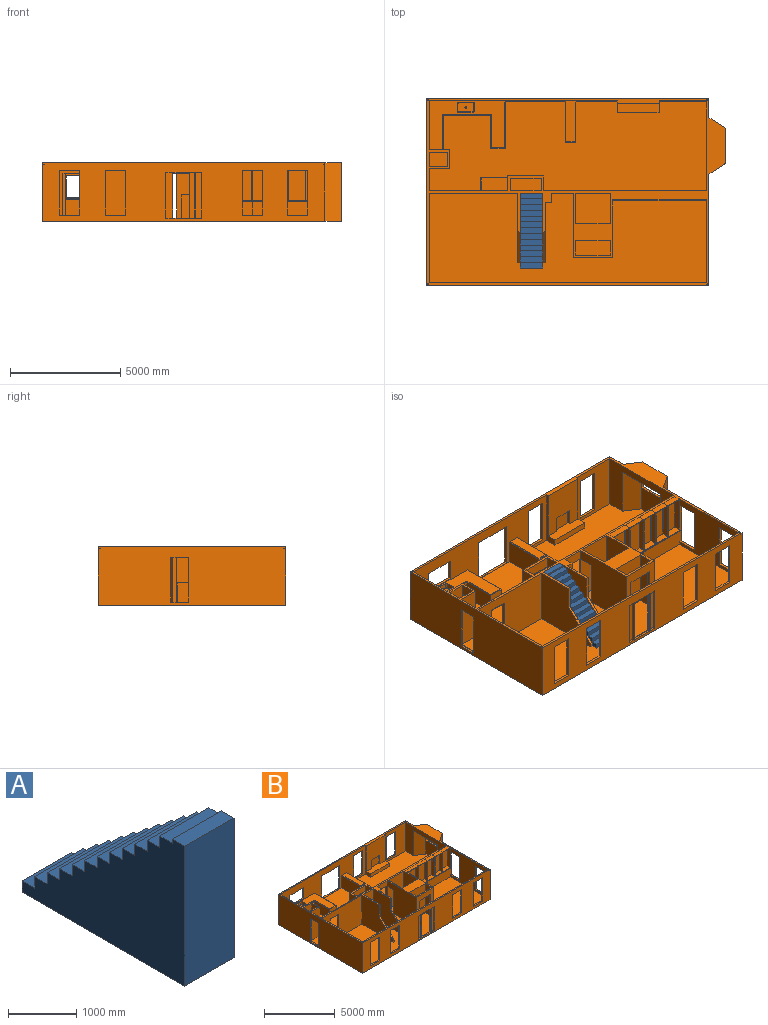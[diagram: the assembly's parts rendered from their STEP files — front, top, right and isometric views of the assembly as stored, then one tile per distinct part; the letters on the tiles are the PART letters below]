
ASSEMBLY  parts=2 mates=1
PART A: 30 faces, bbox 1019.2x3384.6x2514.6 mm
  f0: plane 1019.18x203.2mm, normal (0,1,0), area 207096.4mm2, adj f1,f3,f5,f6
  f1: plane 3384.55x2514.6mm, normal (-1,0,0), area 4781119.5mm2, adj f0,f2,f4,f5,f6,f7,f8,f9
  f2: plane 2514.6x1019.18mm, normal (0,-1,0), area 2562817.5mm2, adj f1,f3,f4,f5
  f3: plane 3384.55x2514.6mm, normal (1,0,0), area 4781119.5mm2, adj f0,f2,f4,f5,f6,f7,f8,f9
  f4: plane 1019.18x260.35mm, normal (0,0,1), area 265342.2mm2, adj f1,f2,f3,f7
  f5: plane 3384.55x1019.18mm, normal (0,0,-1), area 3449448.7mm2, adj f0,f1,f2,f3
  f6: plane 1019.18x260.35mm, normal (0,0,1), area 265342.2mm2, adj f0,f1,f3,f29
  f7: plane 1019.18x76.2mm, normal (0,1,0), area 77661.1mm2, adj f1,f3,f4,f8
  f8: plane 1019.18x260.35mm, normal (0,0,1), area 265342.2mm2, adj f1,f3,f7,f9
  f9: plane 1019.18x203.2mm, normal (0,1,0), area 207096.4mm2, adj f1,f3,f8,f10
  f10: plane 1019.18x260.35mm, normal (0,0,1), area 265342.2mm2, adj f1,f3,f9,f11
  f11: plane 1019.18x203.2mm, normal (0,1,0), area 207096.4mm2, adj f1,f3,f10,f12
  f12: plane 1019.18x260.35mm, normal (0,0,1), area 265342.2mm2, adj f1,f3,f11,f13
  f13: plane 1019.18x203.2mm, normal (0,1,0), area 207096.4mm2, adj f1,f3,f12,f14
  f14: plane 1019.18x260.35mm, normal (0,0,1), area 265342.2mm2, adj f1,f3,f13,f15
  f15: plane 1019.18x203.2mm, normal (0,1,0), area 207096.4mm2, adj f1,f3,f14,f16
  f16: plane 1019.18x260.35mm, normal (0,0,1), area 265342.2mm2, adj f1,f3,f15,f17
  f17: plane 1019.18x203.2mm, normal (0,1,0), area 207096.4mm2, adj f1,f3,f16,f18
  f18: plane 1019.18x260.35mm, normal (0,0,1), area 265342.2mm2, adj f1,f3,f17,f19
  f19: plane 1019.18x203.2mm, normal (0,1,0), area 207096.4mm2, adj f1,f3,f18,f20
  f20: plane 1019.18x260.35mm, normal (0,0,1), area 265342.2mm2, adj f1,f3,f19,f21
  f21: plane 1019.18x203.2mm, normal (0,1,0), area 207096.4mm2, adj f1,f3,f20,f22
  f22: plane 1019.18x260.35mm, normal (0,0,1), area 265342.2mm2, adj f1,f3,f21,f23
  f23: plane 1019.18x203.2mm, normal (0,1,0), area 207096.4mm2, adj f1,f3,f22,f24
  f24: plane 1019.18x260.35mm, normal (0,0,1), area 265342.2mm2, adj f1,f3,f23,f25
  f25: plane 1019.18x203.2mm, normal (0,1,0), area 207096.4mm2, adj f1,f3,f24,f26
  f26: plane 1019.18x260.35mm, normal (0,0,1), area 265342.2mm2, adj f1,f3,f25,f27
  f27: plane 1019.18x203.2mm, normal (0,1,0), area 207096.4mm2, adj f1,f3,f26,f28
  f28: plane 1019.18x260.35mm, normal (0,0,1), area 265342.2mm2, adj f1,f3,f27,f29
  f29: plane 1019.18x203.2mm, normal (0,1,0), area 207096.4mm2, adj f1,f3,f6,f28
PART B: 232 faces, bbox 13538.2x8470.9x2628.9 mm
  f0: plane 1695.45x304.8mm, normal (1,0,0), area 516773.2mm2, adj f12,f218,f221,f230
  f1: plane 1695.45x304.8mm, normal (-1,0,0), area 516773.2mm2, adj f55,f218,f221,f231
  f2: plane 1695.45x304.8mm, normal (-1,0,0), area 516773.2mm2, adj f12,f218,f221,f230
  f3: plane 1695.45x304.8mm, normal (1,0,0), area 516773.2mm2, adj f10,f218,f221,f229
  f4: plane 1695.45x304.8mm, normal (-1,0,0), area 516773.2mm2, adj f10,f218,f221,f229
  f5: plane 1695.45x304.8mm, normal (1,0,0), area 516773.2mm2, adj f9,f218,f221,f228
  f6: plane 1695.45x304.8mm, normal (-1,0,0), area 516773.2mm2, adj f9,f218,f221,f228
  f7: plane 1695.45x304.8mm, normal (1,0,0), area 516773.2mm2, adj f8,f218,f221,f227
  f8: plane 1695.45x730.25mm, normal (0,-1,0), area 1238102.2mm2, adj f7,f218,f223,f227
  f9: plane 1695.45x749.3mm, normal (0,-1,0), area 1270400.7mm2, adj f5,f6,f218,f228
  f10: plane 1695.45x736.6mm, normal (0,-1,0), area 1248868.5mm2, adj f3,f4,f218,f229
  f11: plane 2609.85x2514.6mm, normal (1,0,0), area 6561467.4mm2, adj f14,f29,f54,f200,f216,f217,f218,f219
  f12: plane 1695.45x889mm, normal (0,-1,0), area 1507255mm2, adj f0,f2,f218,f230
  f13: plane 3759.2x2514.6mm, normal (-1,0,0), area 5736762.7mm2, adj f14,f26,f29,f198,f199,f201,f202,f203
  f14: plane 13309.6x8242.3mm, normal (0,0,1), area 92807452.3mm2, adj f11,f13,f15,f16,f17,f21,f22,f26
  f15: plane 3568.7x2514.6mm, normal (0,1,0), area 6190955.4mm2, adj f14,f16,f29,f31,f72,f73,f74,f210
  f16: plane 2514.6x666.75mm, normal (-1,0,0), area 1121449.4mm2, adj f14,f15,f29,f63,f211,f212,f213
  f17: plane 1460.5x1171.91mm, normal (-1,0,0), area 1711580mm2, adj f14,f89,f90,f207
  f18: plane 1460.5x62.35mm, normal (-1,0,0), area 91056.8mm2, adj f89,f90,f91,f209
  f19: plane 5043.5x2628.9mm, normal (1,0,0), area 9542743.4mm2, adj f25,f29,f56,f181,f198,f199,f201,f202
  f20: plane 12788.9x2628.9mm, normal (0,1,0), area 24988966mm2, adj f29,f30,f59,f113,f114,f115,f116,f149
  f21: plane 8521.7x2514.6mm, normal (0,-1,0), area 11001332.7mm2, adj f14,f23,f24,f29,f104,f109,f110,f111
  f22: plane 2514.6x2146.3mm, normal (0,-1,0), area 3539025.2mm2, adj f14,f29,f32,f105,f167,f168,f169,f170
  f23: plane 3435.35x2203.45mm, normal (0,0,1), area 3658851.1mm2, adj f21,f24,f60,f158,f159,f160,f161,f163
  f24: plane 2203.45x1612.9mm, normal (1,0,0), area 3553944.5mm2, adj f21,f23,f29,f60
  f25: plane 12788.9x2628.9mm, normal (0,-1,0), area 22922373.5mm2, adj f19,f29,f30,f82,f83,f84,f85,f92
  f26: plane 12560.3x2514.6mm, normal (0,1,0), area 22139955.7mm2, adj f13,f14,f29,f69,f82,f83,f84,f85
  f27: plane 136.53x114.3mm, normal (0,-1,0), area 15604.8mm2, adj f14,f45,f46,f123
  f28: plane 136.53x114.3mm, normal (0,-1,0), area 15604.8mm2, adj f14,f48,f49,f122
  f29: plane 13538.2x8470.9mm, normal (0,0,1), area 12409928.7mm2, adj f11,f13,f15,f16,f19,f20,f21,f22
  f30: plane 8470.9x2628.9mm, normal (-1,0,0), area 20630442.6mm2, adj f20,f25,f29,f117,f118,f119,f120,f181
  f31: plane 2514.6x996.95mm, normal (1,0,0), area 868224.1mm2, adj f14,f15,f29,f64,f117,f118,f119,f120
  f32: plane 4064x2514.6mm, normal (-1,0,0), area 4954828.8mm2, adj f14,f22,f29,f61,f89,f90,f91
  f33: plane 2514.6x863.6mm, normal (1,0,0), area 932901.7mm2, adj f14,f29,f60,f64,f86,f87,f88
  f34: plane 2514.6x1397mm, normal (0,-1,0), area 1087094.6mm2, adj f14,f29,f41,f43,f79,f80,f81
  f35: plane 2514.6x1549.4mm, normal (0,1,0), area 1439997.1mm2, adj f14,f29,f36,f37,f76,f77,f78
  f36: plane 2514.6x647.7mm, normal (-1,0,0), area 1628706.4mm2, adj f14,f29,f35,f71
  f37: plane 2514.6x647.7mm, normal (1,0,0), area 1628706.4mm2, adj f14,f29,f35,f71
  f38: plane 2514.6x1384.3mm, normal (1,0,0), area 2113221.6mm2, adj f14,f29,f39,f68,f102,f103
  f39: plane 2514.6x1663.7mm, normal (0,-1,0), area 4128378.8mm2, adj f14,f29,f38,f40,f53,f103
  f40: plane 2514.6x1384.3mm, normal (-1,0,0), area 3480960.8mm2, adj f14,f29,f39,f68
  f41: plane 2514.6x552.45mm, normal (-1,0,0), area 1389190.8mm2, adj f14,f29,f34,f42
  f42: plane 2514.6x1397mm, normal (0,1,0), area 3512896.2mm2, adj f14,f29,f41,f43
  f43: plane 2514.6x552.45mm, normal (1,0,0), area 1389190.8mm2, adj f14,f29,f34,f42
  f44: plane 4013.2x2514.6mm, normal (0,-1,0), area 8419338mm2, adj f14,f29,f45,f69,f72,f73,f74
  f45: plane 3149.6x2514.6mm, normal (-1,0,0), area 5509767.2mm2, adj f14,f27,f29,f44,f123,f124
  f46: plane 3149.6x2514.6mm, normal (1,0,0), area 5509767.2mm2, adj f14,f27,f29,f47,f123,f124
  f47: plane 2514.6x1022.35mm, normal (0,-1,0), area 2570801.5mm2, adj f14,f29,f46,f48
  f48: plane 3149.6x2514.6mm, normal (-1,0,0), area 5509767.2mm2, adj f14,f28,f29,f47,f121,f122
  f49: plane 2717.8x2514.6mm, normal (1,0,0), area 4423962.9mm2, adj f14,f28,f29,f50,f121,f122
  f50: plane 2514.6x273.05mm, normal (0,-1,0), area 686611.5mm2, adj f14,f29,f49,f51
  f51: plane 2514.6x546.1mm, normal (1,0,0), area 1320965.1mm2, adj f14,f29,f50,f52,f61,f75
  f52: plane 996.95x457.2mm, normal (0,-1,0), area 455805.5mm2, adj f29,f51,f53,f75
  f53: plane 3028.95x2514.6mm, normal (-1,0,0), area 6196600.5mm2, adj f14,f29,f39,f52,f54,f61,f75,f102
  f54: plane 2514.6x1778mm, normal (0,-1,0), area 2014834.7mm2, adj f11,f14,f29,f53,f76,f77,f78
  f55: plane 1695.45x1028.7mm, normal (0,-1,0), area 1744109.4mm2, adj f1,f218,f222,f231
  f56: plane 2628.9x749.3mm, normal (0.55,-0.84,0), area 2352127.5mm2, adj f19,f29,f57,f181
  f57: plane 2628.9x1584.29mm, normal (1,0,0), area 2814367.8mm2, adj f29,f56,f58,f181,f206,f207,f208,f209
  f58: plane 2628.9x749.3mm, normal (0.55,0.84,0), area 2352127.5mm2, adj f29,f57,f59,f181
  f59: plane 2628.9x865.2mm, normal (1,0,0), area 2274532.1mm2, adj f20,f29,f58,f181
  f60: plane 2514.6x915.15mm, normal (0,1,0), area 1728976.2mm2, adj f14,f23,f24,f29,f33,f153,f197
  f61: plane 7366x2514.6mm, normal (0,1,0), area 16471418.7mm2, adj f14,f29,f32,f51,f53,f62,f75
  f62: plane 2514.6x666.75mm, normal (1,0,0), area 1676609.5mm2, adj f14,f29,f61,f63
  f63: plane 2514.6x1625.6mm, normal (0,1,0), area 1661932.2mm2, adj f14,f16,f29,f62,f79,f80,f81
  f64: plane 2514.6x914.4mm, normal (0,-1,0), area 2299350.2mm2, adj f14,f29,f31,f33
  f65: plane 2514.6x826.73mm, normal (0,-1,0), area 2078905.6mm2, adj f14,f29,f66,f70
  f66: plane 2514.6x635mm, normal (-1,0,0), area 358063.8mm2, adj f14,f29,f65,f67,f86,f87,f88
  f67: plane 2514.6x826.73mm, normal (0,1,0), area 2078905.6mm2, adj f14,f29,f66,f70
  f68: plane 2514.6x1549.4mm, normal (0,1,0), area 3896121.2mm2, adj f14,f29,f38,f40
  f69: plane 4064x2514.6mm, normal (1,0,0), area 10219334.4mm2, adj f14,f26,f29,f44
  f70: plane 2514.6x635mm, normal (1,0,0), area 1596771mm2, adj f14,f29,f65,f67
  f71: plane 2514.6x1549.4mm, normal (0,-1,0), area 3896121.2mm2, adj f14,f29,f36,f37
  f72: plane 2057.4x114.3mm, normal (1,0,0), area 235160.8mm2, adj f14,f15,f44,f74
  f73: plane 2057.4x114.3mm, normal (-1,0,0), area 235160.8mm2, adj f14,f15,f44,f74
  f74: plane 812.8x114.3mm, normal (0,0,-1), area 92903mm2, adj f15,f44,f72,f73
  f75: plane 996.95x114.3mm, normal (0,0,-1), area 113951.4mm2, adj f51,f52,f53,f61
  f76: plane 2057.4x114.3mm, normal (1,0,0), area 235160.8mm2, adj f14,f35,f54,f78
  f77: plane 2057.4x114.3mm, normal (-1,0,0), area 235160.8mm2, adj f14,f35,f54,f78
  f78: plane 1193.8x114.3mm, normal (0,0,-1), area 136451.3mm2, adj f35,f54,f76,f77
  f79: plane 2032x114.3mm, normal (-1,0,0), area 232257.6mm2, adj f14,f34,f63,f81
  f80: plane 2032x114.3mm, normal (1,0,0), area 232257.6mm2, adj f14,f34,f63,f81
  f81: plane 1193.8x114.3mm, normal (0,0,-1), area 136451.3mm2, adj f34,f63,f79,f80
  f82: plane 2057.4x114.3mm, normal (1,0,0), area 235160.8mm2, adj f25,f26,f83,f85
  f83: plane 977.9x114.3mm, normal (0,0,1), area 111774mm2, adj f25,f26,f82,f84
  f84: plane 2057.4x114.3mm, normal (-1,0,0), area 235160.8mm2, adj f25,f26,f83,f85
  f85: plane 977.9x114.3mm, normal (0,0,-1), area 111774mm2, adj f25,f26,f82,f84
  f86: plane 2032x87.78mm, normal (0,1,0), area 178360.8mm2, adj f14,f33,f66,f88
  f87: plane 2032x88.3mm, normal (0,-1,0), area 179434.8mm2, adj f14,f33,f66,f88
  f88: plane 609.6x88.3mm, normal (0,0,-1), area 53669.3mm2, adj f33,f66,f86,f87
  f89: plane 2159x749.3mm, normal (-0.55,0.84,0), area 1931698.9mm2, adj f14,f17,f18,f32,f91,f208
  f90: plane 2159x749.3mm, normal (-0.55,-0.84,0), area 1931698.9mm2, adj f14,f17,f18,f32,f91,f206
  f91: plane 2438.4x749.3mm, normal (0,0,-1), area 1460722.9mm2, adj f18,f32,f89,f90
  f92: plane 304.8x101.6mm, normal (0,0,-1), area 30967.7mm2, adj f25,f93,f95,f96
  f93: plane 2057.4x101.6mm, normal (1,0,0), area 209031.8mm2, adj f25,f92,f94,f96
  f94: plane 304.8x101.6mm, normal (0,0,1), area 30967.7mm2, adj f25,f93,f95,f96
  f95: plane 2057.4x101.6mm, normal (-1,0,0), area 209031.8mm2, adj f25,f92,f94,f96
  f96: plane 2057.4x304.8mm, normal (0,-1,0), area 627095.5mm2, adj f92,f93,f94,f95
  f97: plane 304.8x101.6mm, normal (0,0,1), area 30967.7mm2, adj f25,f98,f100,f101
  f98: plane 2057.4x101.6mm, normal (-1,0,0), area 209031.8mm2, adj f25,f97,f99,f101
  f99: plane 304.8x101.6mm, normal (0,0,-1), area 30967.7mm2, adj f25,f98,f100,f101
  f100: plane 2057.4x101.6mm, normal (1,0,0), area 209031.8mm2, adj f25,f97,f99,f101
  f101: plane 2057.4x304.8mm, normal (0,-1,0), area 627095.5mm2, adj f97,f98,f99,f100
  f102: plane 2032x114.3mm, normal (0,1,0), area 232257.6mm2, adj f14,f38,f53,f103
  f103: plane 673.1x114.3mm, normal (0,0,-1), area 76935.3mm2, adj f38,f39,f53,f102
  f104: plane 2514.6x533.4mm, normal (-1,0,0), area 393023.4mm2, adj f14,f21,f29,f106,f107,f108
  f105: plane 2514.6x533.4mm, normal (1,0,0), area 393023.4mm2, adj f14,f22,f29,f106,f107,f108
  f106: plane 2228.85x1892.3mm, normal (0,-1,0), area 3618107.4mm2, adj f29,f104,f105,f107,f186,f187,f188
  f107: plane 1892.3x527.05mm, normal (0,0,1), area 888949.8mm2, adj f104,f105,f106,f108,f186,f188,f189
  f108: plane 1892.3x285.75mm, normal (0,-1,0), area 540724.7mm2, adj f14,f104,f105,f107
  f109: plane 1866.9x1066.8mm, normal (1,0,0), area 1991608.9mm2, adj f14,f21,f112,f192
  f110: plane 1841.5x438.15mm, normal (0,0,1), area 806853.2mm2, adj f21,f190,f191,f192
  f111: plane 1866.9x1066.8mm, normal (-1,0,0), area 1991608.9mm2, adj f14,f21,f112,f190
  f112: plane 1066.8x488.95mm, normal (0,-1,0), area 521611.9mm2, adj f14,f109,f111,f191
  f113: plane 1787.53x114.3mm, normal (0,0,1), area 204314.1mm2, adj f20,f21,f114,f116
  f114: plane 2012.95x114.3mm, normal (-1,0,0), area 230080.2mm2, adj f20,f21,f113,f115
  f115: plane 1787.53x114.3mm, normal (0,0,-1), area 204314.1mm2, adj f20,f21,f114,f116
  f116: plane 2012.95x114.3mm, normal (1,0,0), area 230080.2mm2, adj f20,f21,f113,f115
  f117: plane 2032x114.3mm, normal (0,-1,0), area 232257.6mm2, adj f30,f31,f118,f120
  f118: plane 806.45x114.3mm, normal (0,0,-1), area 92177.2mm2, adj f30,f31,f117,f119
  f119: plane 2032x114.3mm, normal (0,1,0), area 232257.6mm2, adj f30,f31,f118,f120
  f120: plane 806.45x114.3mm, normal (0,0,1), area 92177.2mm2, adj f30,f31,f117,f119
  f121: plane 1041.4x114.3mm, normal (0,-1,0), area 119032mm2, adj f29,f48,f49,f122
  f122: plane 1409.7x1336.68mm, normal (0,-0.69,0.73), area 222046.8mm2, adj f28,f48,f49,f121
  f123: plane 1409.7x1336.68mm, normal (0,-0.69,0.73), area 222046.8mm2, adj f27,f45,f46,f124
  f124: plane 1041.4x114.3mm, normal (0,-1,0), area 119032mm2, adj f29,f45,f46,f123
  f125: cylinder r=31.75mm len=63.5mm, axis (0,0,1), area 10134.1mm2, adj f29,f126
  f126: plane 63.5x63.5mm, normal (0,0,1), area 3166.9mm2, adj f125
  f127: cylinder r=31.75mm len=63.5mm, axis (0,0,1), area 10134.1mm2, adj f29,f128
  f128: plane 63.5x63.5mm, normal (0,0,1), area 3166.9mm2, adj f127
  f129: cylinder r=31.75mm len=63.5mm, axis (0,0,1), area 10134.1mm2, adj f29,f130
  f130: plane 63.5x63.5mm, normal (0,0,1), area 3166.9mm2, adj f129
  f131: cylinder r=31.75mm len=63.5mm, axis (0,0,1), area 10134.1mm2, adj f29,f132
  f132: plane 63.5x63.5mm, normal (0,0,1), area 3166.9mm2, adj f131
  f133: plane 914.4x114.3mm, normal (0,0,1), area 104515.9mm2, adj f25,f26,f134,f136
  f134: plane 2032x114.3mm, normal (1,0,0), area 232257.6mm2, adj f25,f26,f133,f135
  f135: plane 914.4x114.3mm, normal (0,0,-1), area 104515.9mm2, adj f25,f26,f134,f136
  f136: plane 2032x114.3mm, normal (-1,0,0), area 232257.6mm2, adj f25,f26,f133,f135
  f137: plane 914.4x114.3mm, normal (0,0,-1), area 104515.9mm2, adj f25,f26,f138,f140
  f138: plane 2032x114.3mm, normal (-1,0,0), area 232257.6mm2, adj f25,f26,f137,f139
  f139: plane 914.4x114.3mm, normal (0,0,1), area 104515.9mm2, adj f25,f26,f138,f140
  f140: plane 2032x114.3mm, normal (1,0,0), area 232257.6mm2, adj f25,f26,f137,f139
  f141: plane 914.4x114.3mm, normal (0,0,-1), area 104515.9mm2, adj f25,f26,f142,f144
  f142: plane 2032x114.3mm, normal (-1,0,0), area 232257.6mm2, adj f25,f26,f141,f143
  f143: plane 914.4x114.3mm, normal (0,0,1), area 104515.9mm2, adj f25,f26,f142,f144
  f144: plane 2032x114.3mm, normal (1,0,0), area 232257.6mm2, adj f25,f26,f141,f143
  f145: plane 2032x114.3mm, normal (1,0,0), area 232257.6mm2, adj f25,f26,f146,f148
  f146: plane 914.4x114.3mm, normal (0,0,-1), area 104515.9mm2, adj f25,f26,f145,f147
  f147: plane 2032x114.3mm, normal (-1,0,0), area 232257.6mm2, adj f25,f26,f146,f148
  f148: plane 914.4x114.3mm, normal (0,0,1), area 104515.9mm2, adj f25,f26,f145,f147
  f149: plane 1377.95x114.3mm, normal (0,0,-1), area 157499.7mm2, adj f20,f21,f150,f152
  f150: plane 960.78x114.3mm, normal (1,0,0), area 109817mm2, adj f20,f21,f149,f151
  f151: plane 1377.95x114.3mm, normal (0,0,1), area 157499.7mm2, adj f20,f21,f150,f152
  f152: plane 960.78x114.3mm, normal (-1,0,0), area 109817mm2, adj f20,f21,f149,f151
  f153: plane 1568.45x876.3mm, normal (1,0,0), area 1374432.7mm2, adj f14,f60,f155,f197
  f154: plane 2146.3x876.3mm, normal (1,0,0), area 1880802.7mm2, adj f14,f21,f157,f193
  f155: plane 2149.48x876.3mm, normal (0,-1,0), area 1883584.9mm2, adj f14,f153,f156,f196
  f156: plane 1511.3x876.3mm, normal (-1,0,0), area 1324352.2mm2, adj f14,f155,f157,f195
  f157: plane 876.3x676.28mm, normal (0,-1,0), area 592619.8mm2, adj f14,f154,f156,f194
  f158: plane 324.73x228.6mm, normal (1,0,0), area 74232.9mm2, adj f23,f163,f166,f176
  f159: plane 660.4x228.6mm, normal (0,1,0), area 150967.4mm2, adj f23,f163,f164,f177
  f160: plane 324.73x228.6mm, normal (-1,0,0), area 74232.9mm2, adj f23,f164,f165,f173
  f161: plane 660.4x228.6mm, normal (0,-1,0), area 150967.4mm2, adj f23,f165,f166,f172
  f162: plane 736.6x400.93mm, normal (0,0,1), area 289517.4mm2, adj f171,f172,f173,f174,f175,f176,f177,f178
  f163: cylinder r=63.5mm len=228.6mm, axis (0,0,1), area 22801.8mm2, adj f23,f158,f159,f178
  f164: cylinder r=63.5mm len=228.6mm, axis (0,0,-1), area 22801.8mm2, adj f23,f159,f160,f175
  f165: cylinder r=63.5mm len=228.6mm, axis (0,0,1), area 22801.8mm2, adj f23,f160,f161,f171
  f166: cylinder r=63.5mm len=228.6mm, axis (0,0,-1), area 22801.8mm2, adj f23,f158,f161,f174
  f167: plane 2032x114.3mm, normal (-1,0,0), area 232257.6mm2, adj f20,f22,f168,f170
  f168: plane 914.4x114.3mm, normal (0,0,-1), area 104515.9mm2, adj f20,f22,f167,f169
  f169: plane 2032x114.3mm, normal (1,0,0), area 232257.6mm2, adj f20,f22,f168,f170
  f170: plane 914.4x114.3mm, normal (0,0,1), area 104515.9mm2, adj f20,f22,f167,f169
  f171: torus R=38.1mm, axis (0,0,1), area 3401.2mm2, adj f162,f165,f172,f173
  f172: cylinder r=25.4mm len=660.4mm, axis (-1,0,0), area 26348.8mm2, adj f161,f162,f171,f174
  f173: cylinder r=25.4mm len=324.73mm, axis (0,1,0), area 12956.1mm2, adj f160,f162,f171,f175
  f174: torus R=38.1mm, axis (0,0,1), area 3401.2mm2, adj f162,f166,f172,f176
  f175: torus R=38.1mm, axis (0,0,1), area 3401.2mm2, adj f162,f164,f173,f177
  f176: cylinder r=25.4mm len=324.73mm, axis (0,-1,0), area 12956.1mm2, adj f158,f162,f174,f178
  f177: cylinder r=25.4mm len=660.4mm, axis (1,0,0), area 26348.8mm2, adj f159,f162,f175,f178
  f178: torus R=38.1mm, axis (0,0,1), area 3401.2mm2, adj f162,f163,f176,f177
  f179: cylinder r=38.1mm len=76.2mm, axis (0,0,1), area 6080.5mm2, adj f162,f180
  f180: plane 76.2x76.2mm, normal (0,0,1), area 4560.4mm2, adj f179
  f181: plane 13538.2x8470.9mm, normal (0,0,-1), area 109886974.8mm2, adj f19,f20,f25,f30,f56,f57,f58,f59
  f182: plane 2032x114.3mm, normal (1,0,0), area 232257.6mm2, adj f20,f21,f183,f185
  f183: plane 911.23x114.3mm, normal (0,0,1), area 104153mm2, adj f20,f21,f182,f184
  f184: plane 2032x114.3mm, normal (-1,0,0), area 232257.6mm2, adj f20,f21,f183,f185
  f185: plane 911.23x114.3mm, normal (0,0,-1), area 104153mm2, adj f20,f21,f182,f184
  f186: plane 726.28x101.6mm, normal (-1,0,0), area 73790.2mm2, adj f106,f107,f187,f189
  f187: plane 825.5x101.6mm, normal (0,0,-1), area 83870.8mm2, adj f106,f186,f188,f189
  f188: plane 726.28x101.6mm, normal (1,0,0), area 73790.2mm2, adj f106,f107,f187,f189
  f189: plane 825.5x726.28mm, normal (0,-1,0), area 599545.4mm2, adj f107,f186,f187,f188
  f190: plane 1866.9x25.4mm, normal (-0.71,0,0.71), area 66604.8mm2, adj f21,f110,f111,f191
  f191: plane 488.95x25.4mm, normal (0,-0.71,0.71), area 16651.2mm2, adj f110,f112,f190,f192
  f192: plane 1866.9x25.4mm, normal (0.71,0,0.71), area 66604.8mm2, adj f21,f109,f110,f191
  f193: plane 2146.3x25.4mm, normal (0.71,0,0.71), area 76641.1mm2, adj f21,f23,f154,f194
  f194: plane 676.28x25.4mm, normal (0,-0.71,0.71), area 23380.1mm2, adj f23,f157,f193,f195
  f195: plane 1536.7x25.4mm, normal (-0.71,0,0.71), area 54287.4mm2, adj f23,f156,f194,f196
  f196: plane 2200.28x25.4mm, normal (0,-0.71,0.71), area 78123.7mm2, adj f23,f155,f195,f197
  f197: plane 1593.85x25.4mm, normal (0.71,0,0.71), area 56796.5mm2, adj f23,f60,f153,f196
  f198: plane 2032x114.3mm, normal (0,1,0), area 232257.6mm2, adj f13,f19,f199,f201
  f199: plane 914.4x114.3mm, normal (0,0,-1), area 104515.9mm2, adj f13,f19,f198,f221
  f200: plane 1066.8x762mm, normal (0,-1,0), area 812901.6mm2, adj f11,f14,f216,f224
  f201: plane 914.4x114.3mm, normal (0,0,1), area 104515.9mm2, adj f13,f19,f198,f221
  f202: plane 2032x114.3mm, normal (0,1,0), area 232257.6mm2, adj f13,f19,f203,f205
  f203: plane 914.4x114.3mm, normal (0,0,-1), area 104515.9mm2, adj f13,f19,f202,f204
  f204: plane 2032x114.3mm, normal (0,-1,0), area 232257.6mm2, adj f13,f19,f203,f205
  f205: plane 914.4x114.3mm, normal (0,0,1), area 104515.9mm2, adj f13,f19,f202,f204
  f206: plane 924.74x114.3mm, normal (0,-1,0), area 105697.8mm2, adj f57,f90,f207,f209
  f207: plane 1460.5x114.3mm, normal (0,0,1), area 166935.2mm2, adj f17,f57,f206,f208
  f208: plane 924.74x114.3mm, normal (0,1,0), area 105697.8mm2, adj f57,f89,f207,f209
  f209: plane 1460.5x114.3mm, normal (0,0,-1), area 166935.2mm2, adj f18,f57,f206,f208
  f210: plane 885.83x609.6mm, normal (-1,0,0), area 539998.9mm2, adj f14,f15,f212,f214
  f211: plane 1193.8x584.2mm, normal (0,0,1), area 697418mm2, adj f15,f16,f213,f214
  f212: plane 1219.2x885.83mm, normal (0,1,0), area 1079997.8mm2, adj f14,f16,f210,f213
  f213: plane 1219.2x25.4mm, normal (0,0.71,0.71), area 43338.7mm2, adj f16,f211,f212,f214
  f214: plane 609.6x25.4mm, normal (-0.71,0,0.71), area 21441.3mm2, adj f15,f210,f211,f213
  f215: plane 38.1x34.93mm, normal (1,0,0), area 1261.4mm2, adj f216,f217,f218,f219,f220,f221
  f216: plane 4248.15x327.03mm, normal (0,0,-1), area 365382.3mm2, adj f11,f200,f215,f219,f221,f224,f225,f226
  f217: plane 4248.15x12.7mm, normal (0,-1,0), area 53951.5mm2, adj f11,f215,f219,f220
  f218: plane 4248.15x327.03mm, normal (0,0,1), area 1354412.6mm2, adj f0,f1,f2,f3,f4,f5,f6,f7
  f219: cylinder r=12.7mm len=4248.15mm, axis (1,0,0), area 84746.8mm2, adj f11,f215,f216,f217
  f220: cylinder r=12.7mm len=4248.15mm, axis (-1,0,0), area 84746.8mm2, adj f11,f215,f217,f218
  f221: plane 4362.45x2514.6mm, normal (0,-1,0), area 2253745.4mm2, adj f0,f1,f2,f3,f4,f5,f6,f7
  f222: plane 1695.45x304.8mm, normal (1,0,0), area 516773.2mm2, adj f55,f218,f221,f231
  f223: plane 1695.45x304.8mm, normal (-1,0,0), area 516773.2mm2, adj f8,f218,f221,f227
  f224: plane 762x304.8mm, normal (1,0,0), area 232257.6mm2, adj f14,f200,f216,f226
  f225: plane 762x304.8mm, normal (-1,0,0), area 232257.6mm2, adj f14,f216,f221,f226
  f226: plane 889x762mm, normal (0,-1,0), area 677418mm2, adj f14,f216,f224,f225
  f227: plane 730.25x304.8mm, normal (0,0,-1), area 222580.2mm2, adj f7,f8,f221,f223
  f228: plane 749.3x304.8mm, normal (0,0,-1), area 228386.6mm2, adj f5,f6,f9,f221
  f229: plane 736.6x304.8mm, normal (0,0,-1), area 224515.7mm2, adj f3,f4,f10,f221
  f230: plane 889x304.8mm, normal (0,0,-1), area 270967.2mm2, adj f0,f2,f12,f221
  f231: plane 1028.7x304.8mm, normal (0,0,-1), area 313547.8mm2, adj f1,f55,f221,f222
PLACE A rot(axis=(0,0,-1),180deg) t=(-669.18,2019.8,1132.95)mm
PLACE B t=(462.71,-1965.96,1132.95)mm
MATE fastened A.f2 <-> B.f47  axis (0,1,0) through (-1178.77,2019.8,2390.25)mm
